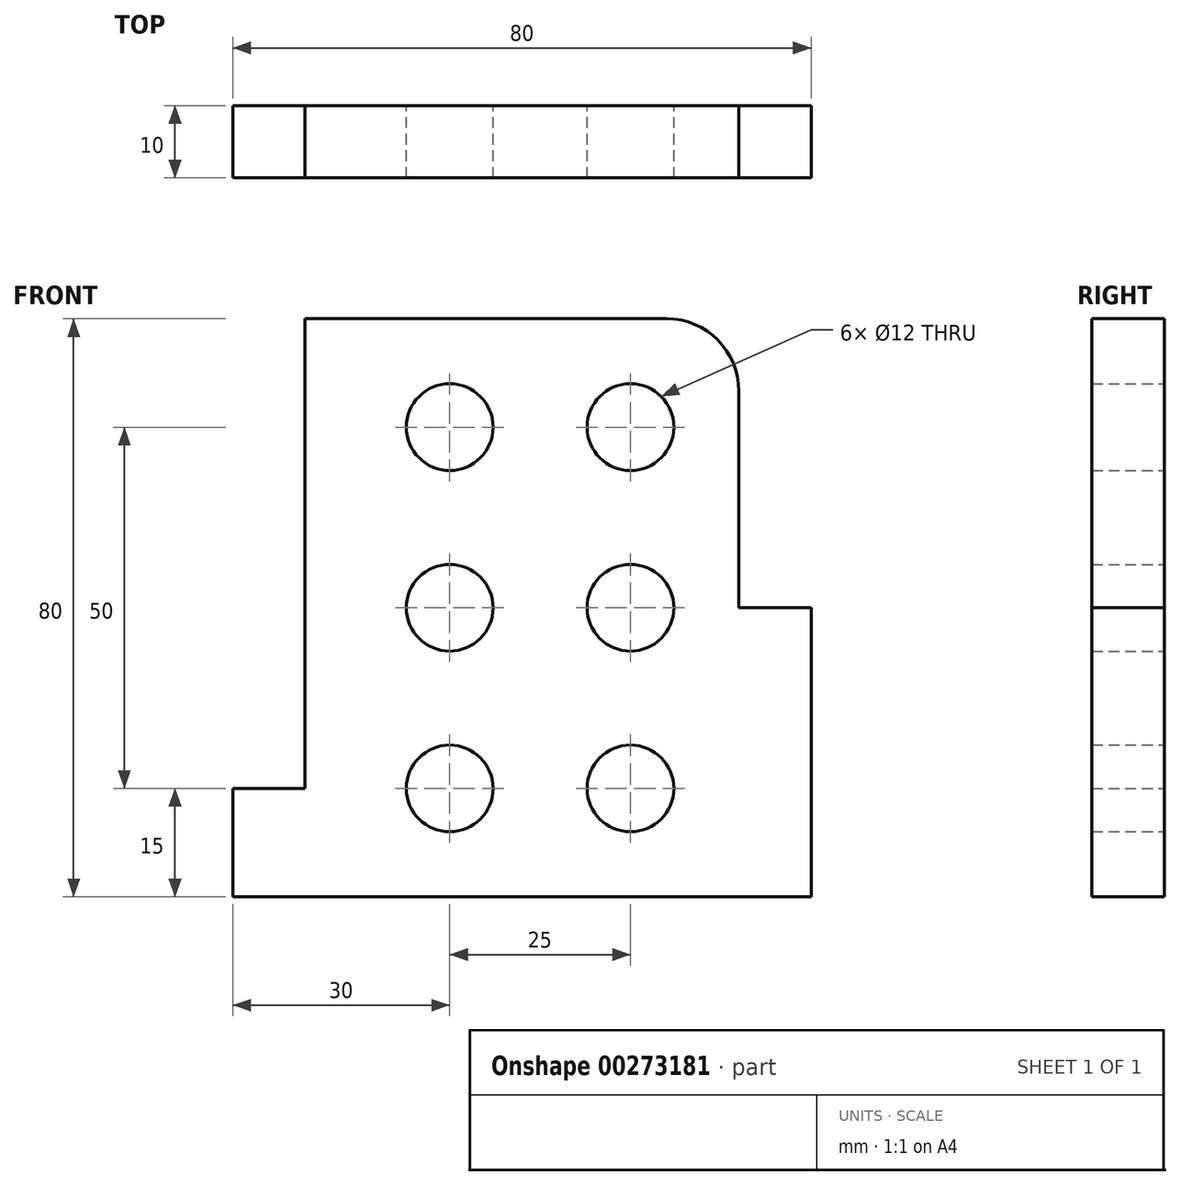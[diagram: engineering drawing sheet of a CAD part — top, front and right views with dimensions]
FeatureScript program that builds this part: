
annotation { "Feature Type Name" : "Feature", "Feature Type Description" : "" }
export const myFeature = defineFeature(function(context is Context, id is Id, definition is map)
    precondition{}
    {
        {
            var Q0;
            Q0=qCreatedBy(makeId("Front.planeOp"),FACE);
            var sketch = newSketch(context, id + "F0", { "sketchPlane" : qUnion([Q0])});
            skLineSegment(sketch, "E0", {"start": v(0, 0) * mm, "end": v(0, 15) * mm});
            skLineSegment(sketch, "E1", {"start": v(0, 15) * mm, "end": v(10, 15) * mm});
            skLineSegment(sketch, "E2", {"start": v(10, 15) * mm, "end": v(10, 80) * mm});
            skLineSegment(sketch, "E3", {"start": v(10, 80) * mm, "end": v(60, 80) * mm});
            skLineSegment(sketch, "E4", {"start": v(70, 70) * mm, "end": v(70, 40) * mm});
            skLineSegment(sketch, "E5", {"start": v(70, 40) * mm, "end": v(80, 40) * mm});
            skLineSegment(sketch, "E6", {"start": v(80, 40) * mm, "end": v(80, 0) * mm});
            skLineSegment(sketch, "E7", {"start": v(80, 0) * mm, "end": v(0, 0) * mm});
            skPoint(sketch, "E8.visualSharp", {"position": v(70, 80) * mm});
            skArc(sketch, "E8.filletArc", {"start": v(70, 70) * mm, "mid": v(67.07, 77.07) * mm, "end": v(60, 80) * mm});
            skCircle(sketch, "E9", {"center": v(30, 65) * mm, "radius": 6 * mm});
            skCircle(sketch, "E10", {"center": v(55, 65) * mm, "radius": 6 * mm});
            skCircle(sketch, "E11", {"center": v(30, 40) * mm, "radius": 6 * mm});
            skCircle(sketch, "E12", {"center": v(55, 40) * mm, "radius": 6 * mm});
            skCircle(sketch, "E13", {"center": v(30, 15) * mm, "radius": 6 * mm});
            skCircle(sketch, "E14", {"center": v(55, 15) * mm, "radius": 6 * mm});
            skPoint(sketch, "E15", {"position": v(75, 40) * mm});
            skSolve(sketch);
        }
        {
            var Q0;
            Q0=makeQuery(id+"F0.imprint","IMPRINT",FACE,{"disambiguationData":[TD([[makeQuery(id+"F0.imprint","IMPRINT",EDGE,{"derivedFrom":sQuery(id+"F0.wireOp",EDGE,"E0")}),-1.0]])]});
            extrude(context, id + "F1", {"entities" : qUnion([Q0]), "depth" : 10 * mm});
        }
    });
